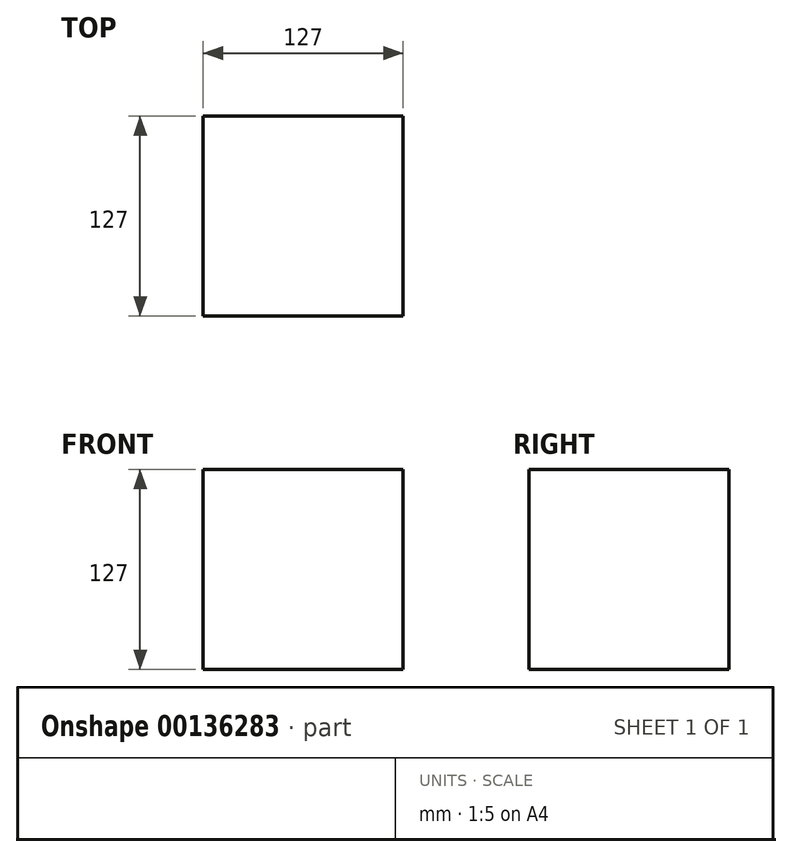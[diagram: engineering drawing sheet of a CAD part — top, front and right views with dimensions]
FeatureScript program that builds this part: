
annotation { "Feature Type Name" : "Feature", "Feature Type Description" : "" }
export const myFeature = defineFeature(function(context is Context, id is Id, definition is map)
    precondition{}
    {
        {
            var Q0;
            Q0=qCreatedBy(makeId("Front.planeOp"),FACE);
            var sketch = newSketch(context, id + "F0", { "sketchPlane" : qUnion([Q0])});
            skLineSegment(sketch, "E0.bottom", {"start": v(-45.59, 78) * mm, "end": v(81.41, 78) * mm});
            skLineSegment(sketch, "E0.top", {"start": v(-45.59, -49) * mm, "end": v(81.41, -49) * mm});
            skLineSegment(sketch, "E0.left", {"start": v(-45.59, 78) * mm, "end": v(-45.59, -49) * mm});
            skLineSegment(sketch, "E0.right", {"start": v(81.41, 78) * mm, "end": v(81.41, -49) * mm});
            skSolve(sketch);
        }
        {
            var Q0;
            Q0 = qSketchRegion(id + "F0", true);
            extrude(context, id + "F1", {"entities" : qUnion([Q0]), "depth" : 127 * mm});
        }
    });
